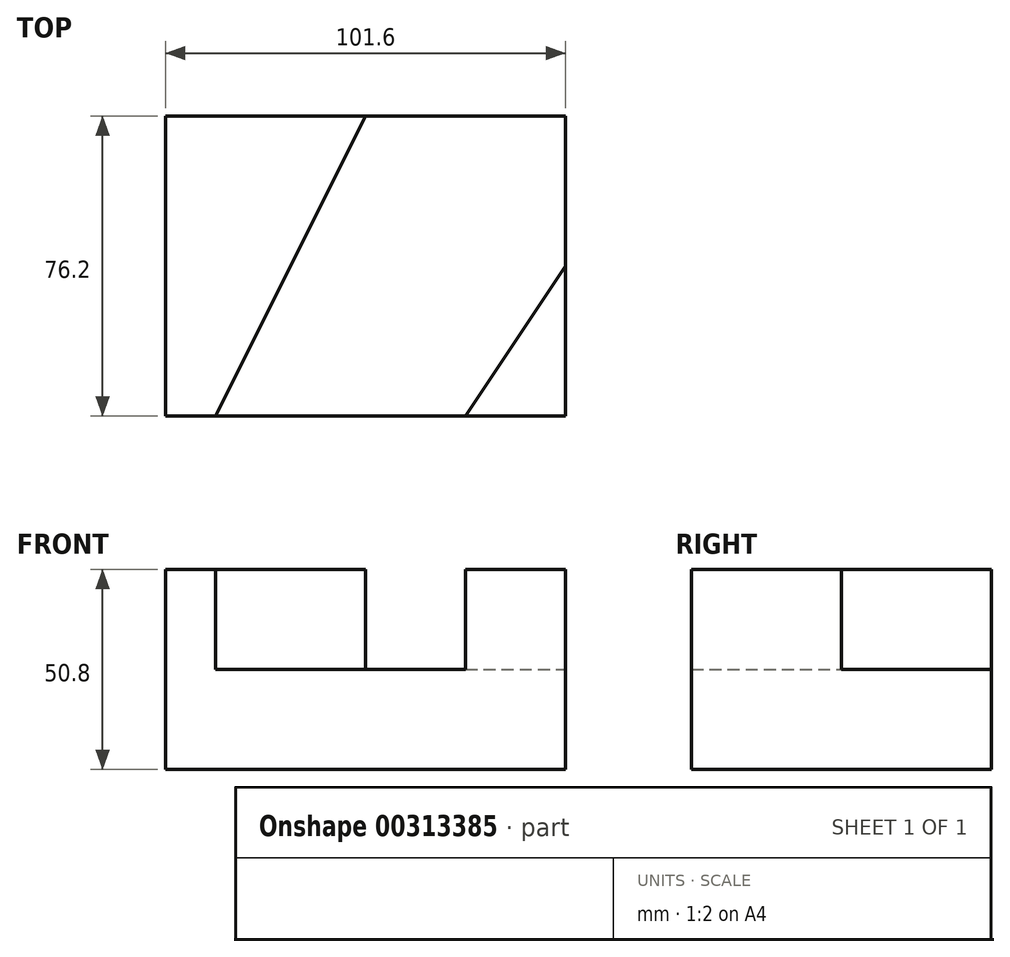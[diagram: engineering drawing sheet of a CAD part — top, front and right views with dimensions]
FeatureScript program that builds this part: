
annotation { "Feature Type Name" : "Feature", "Feature Type Description" : "" }
export const myFeature = defineFeature(function(context is Context, id is Id, definition is map)
    precondition{}
    {
        {
            var Q0;
            Q0=qCreatedBy(makeId("Front.planeOp"),FACE);
            var sketch = newSketch(context, id + "F0", { "sketchPlane" : qUnion([Q0])});
            skLineSegment(sketch, "E0", {"start": v(-45.13, -12.51) * mm, "end": v(-45.13, -37.91) * mm});
            skLineSegment(sketch, "E1", {"start": v(-45.13, -37.91) * mm, "end": v(56.47, -37.91) * mm});
            skLineSegment(sketch, "E2", {"start": v(56.47, -37.91) * mm, "end": v(56.47, -12.51) * mm});
            skLineSegment(sketch, "E3", {"start": v(56.47, -12.51) * mm, "end": v(-45.13, -12.51) * mm});
            skSolve(sketch);
        }
        {
            var Q0;
            Q0 = qSketchRegion(id + "F0", true);
            extrude(context, id + "F1", {"entities" : qUnion([Q0]), "depth" : 76.2 * mm});
        }
        {
            var Q0;
            Q0=makeQuery(id+"F1.opExtrude","SWEPT_FACE",FACE,{"disambiguationData":[OSD([sQuery(id+"F0.wireOp",EDGE,"E3")])]});
            var sketch = newSketch(context, id + "F2", { "sketchPlane" : qUnion([Q0])});
            skLineSegment(sketch, "E4", {"start": v(-45.13, -76.2) * mm, "end": v(-32.43, -76.2) * mm});
            skLineSegment(sketch, "E5", {"start": v(-45.13, -76.2) * mm, "end": v(-45.13, 0) * mm});
            skLineSegment(sketch, "E6", {"start": v(-45.13, 0) * mm, "end": v(5.67, 0) * mm});
            skLineSegment(sketch, "E7", {"start": v(5.67, 0) * mm, "end": v(-32.43, -76.2) * mm});
            skLineSegment(sketch, "E8", {"start": v(56.47, -38.1) * mm, "end": v(56.47, -76.2) * mm});
            skLineSegment(sketch, "E9", {"start": v(56.47, -76.2) * mm, "end": v(31.07, -76.2) * mm});
            skLineSegment(sketch, "E10", {"start": v(31.07, -76.2) * mm, "end": v(56.47, -38.1) * mm});
            skSolve(sketch);
        }
        {
            var Q0;
            Q0 = qSketchRegion(id + "F2", true);
            extrude(context, id + "F3", {"entities" : qUnion([Q0]), "operationType" : NewBodyOperationType.ADD, "depth" : 25.4 * mm});
        }
    });
